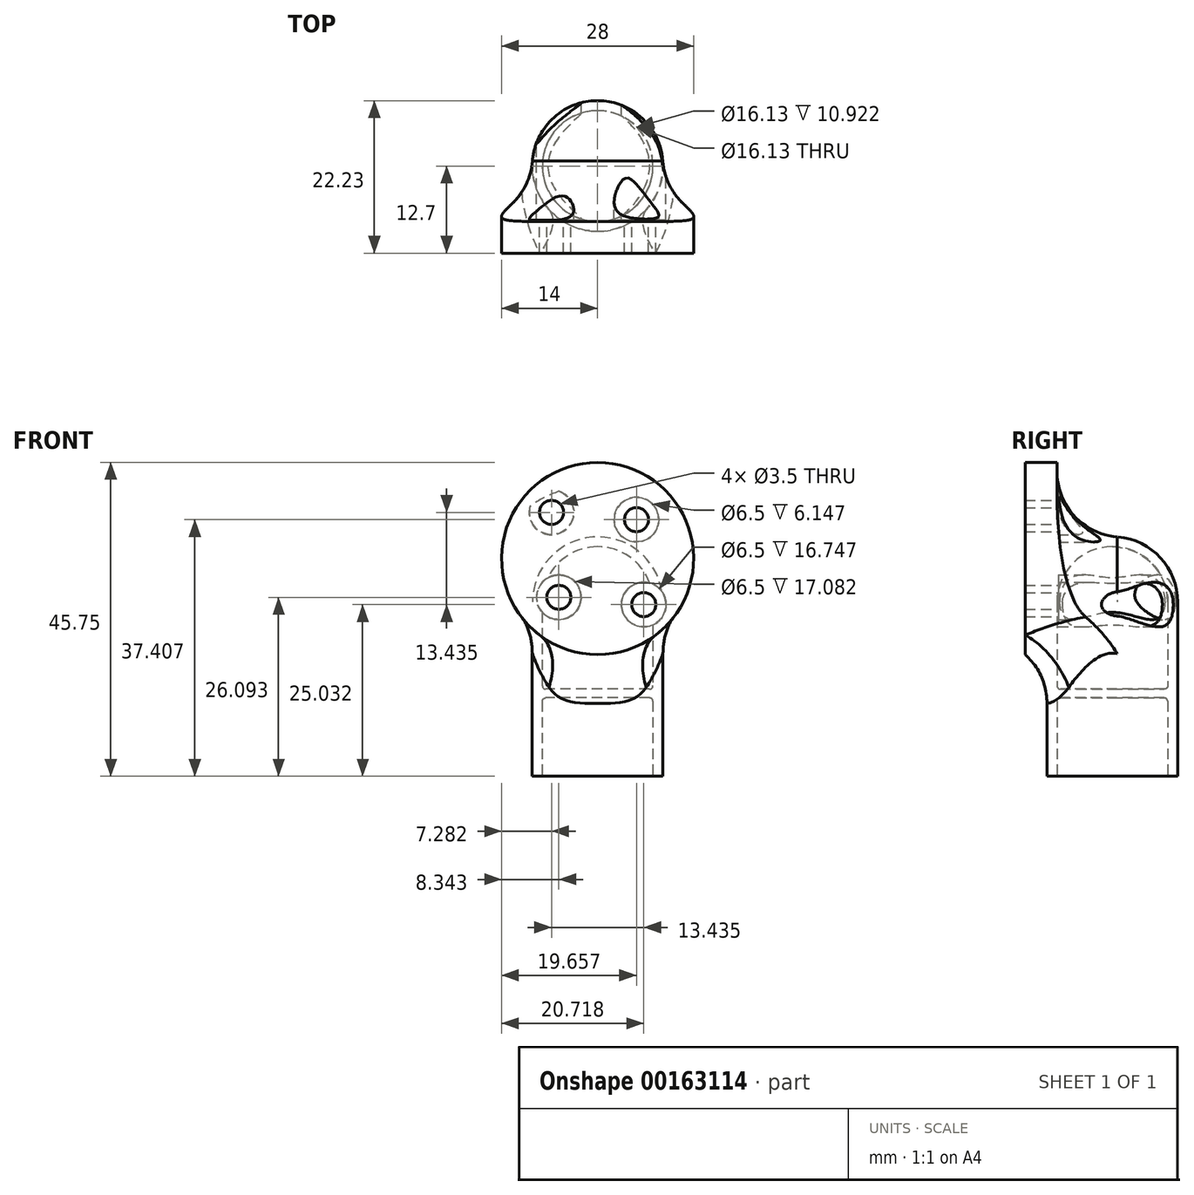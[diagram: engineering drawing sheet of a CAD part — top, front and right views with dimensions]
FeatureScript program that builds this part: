
annotation { "Feature Type Name" : "Feature", "Feature Type Description" : "" }
export const myFeature = defineFeature(function(context is Context, id is Id, definition is map)
    precondition{}
    {
        {
            var Q0;
            Q0=qCreatedBy(makeId("Top.planeOp"),FACE);
            var sketch = newSketch(context, id + "F0", { "sketchPlane" : qUnion([Q0])});
            skCircle(sketch, "E0", {"center": v(0, 0) * mm, "radius": 8.06 * mm});
            skCircle(sketch, "E1", {"center": v(0, 0) * mm, "radius": 9.53 * mm});
            skSolve(sketch);
        }
        {
            var Q0;
            Q0 = qSketchRegion(id + "F0", true);
            extrude(context, id + "F1", {"entities" : qUnion([Q0]), "depth" : 12.7 * mm, "hasSecondDirection" : true, "secondDirectionOppositeDirection" : true, "secondDirectionDepth" : 12.7 * mm});
        }
        {
            var Q0;
            Q0=qCreatedBy(makeId("Front.planeOp"),FACE);
            var sketch = newSketch(context, id + "F2", { "sketchPlane" : qUnion([Q0])});
            skCircle(sketch, "E2", {"center": v(0, 19.05) * mm, "radius": 14 * mm});
            skSolve(sketch);
        }
        {
            var Q0;
            Q0 = qSketchRegion(id + "F2", true);
            extrude(context, id + "F3", {"entities" : qUnion([Q0]), "operationType" : NewBodyOperationType.ADD, "depth" : 12.7 * mm, "hasSecondDirection" : true, "secondDirectionOppositeDirection" : false, "secondDirectionDepth" : 16.13 * mm / 2});
        }
        {
            var Q0;
            Q0=qCreatedBy(makeId("Right.planeOp"),FACE);
            var sketch = newSketch(context, id + "F4", { "sketchPlane" : qUnion([Q0])});
            skLineSegment(sketch, "E3", {"start": v(0, 0) * mm, "end": v(0, 38.72) * mm, "construction": true});
            skArc(sketch, "E4", {"start": v(9.53, 12.7) * mm, "mid": v(6.74, 19.44) * mm, "end": v(0, 22.23) * mm});
            skArc(sketch, "E5", {"start": v(0, 20.76) * mm, "mid": v(5.7, 18.4) * mm, "end": v(8.06, 12.7) * mm});
            skLineSegment(sketch, "E6", {"start": v(9.53, 12.7) * mm, "end": v(8.06, 12.7) * mm});
            skLineSegment(sketch, "E7", {"start": v(0, 22.23) * mm, "end": v(0, 20.76) * mm});
            skSolve(sketch);
        }
        {
            var Q0;
            Q0=qCreatedBy(makeId("Right.planeOp"),FACE);
            var sketch = newSketch(context, id + "F5", { "sketchPlane" : qUnion([Q0])});
            skLineSegment(sketch, "E8", {"start": v(0, 0) * mm, "end": v(0, 27.06) * mm});
            skSolve(sketch);
        }
        {
            var Q0;
            Q0=makeQuery(id+"F4.imprint","IMPRINT",FACE,{"disambiguationData":[TD([[makeQuery(id+"F4.imprint","IMPRINT",EDGE,{"derivedFrom":sQuery(id+"F4.wireOp",EDGE,"E4")}),1.0]])]});
            var Q1;
            Q1=sQuery(id+"F5.wireOp",EDGE,"E8");
            revolve(context, id + "F6", {"operationType" : NewBodyOperationType.ADD, "entities" : qUnion([Q0]), "axis" : qUnion([Q1]), "revolveType" : RevolveType.FULL});
        }
        {
            var Q0;
            Q0=makeQuery(id+"F3.boolean.opBoolean","INTERSECT",EDGE,{"disambiguationData":[OD(1.0)],"derivedFrom":[makeQuery(id+"F1.opExtrude","SWEPT_FACE",FACE,{"disambiguationData":[OSD([sQuery(id+"F0.wireOp",EDGE,"E1")])]}),makeQuery(id+"F3.opExtrude","CAP_FACE",FACE,{"disambiguationData":[OSD([sQuery(id+"F2.wireOp",EDGE,"E2")])],"isStart":true})]});
            fillet(context, id + "F7", {"entities" : qUnion([Q0]), "radius" : 9.52 * mm, "tangentPropagation" : true, "allowEdgeOverflow" : false});
        }
        {
            var Q0;
            Q0=makeQuery(id+"F3.boolean.opBoolean","INTERSECT",EDGE,{"disambiguationData":[OD(1.0)],"derivedFrom":[makeQuery(id+"F1.opExtrude","SWEPT_FACE",FACE,{"disambiguationData":[OSD([sQuery(id+"F0.wireOp",EDGE,"E1")])]}),makeQuery(id+"F3.opExtrude","SWEPT_FACE",FACE,{"disambiguationData":[OSD([sQuery(id+"F2.wireOp",EDGE,"E2")])]})]});
            var Q1;
            Q1=makeQuery(id+"F3.boolean.opBoolean","INTERSECT",EDGE,{"disambiguationData":[OD(0.0)],"derivedFrom":[makeQuery(id+"F1.opExtrude","SWEPT_FACE",FACE,{"disambiguationData":[OSD([sQuery(id+"F0.wireOp",EDGE,"E1")])]}),makeQuery(id+"F3.opExtrude","SWEPT_FACE",FACE,{"disambiguationData":[OSD([sQuery(id+"F2.wireOp",EDGE,"E2")])]})]});
            fillet(context, id + "F8", {"entities" : qUnion([Q0, Q1]), "radius" : 9.52 * mm, "tangentPropagation" : true, "allowEdgeOverflow" : false});
        }
        {
            var Q0;
            Q0=qCreatedBy(makeId("Front.planeOp"),FACE);
            var sketch = newSketch(context, id + "F9", { "sketchPlane" : qUnion([Q0])});
            skCircle(sketch, "E9", {"center": v(0, 19.05) * mm, "radius": 8 * mm, "construction": true});
            skCircle(sketch, "E10", {"center": v(0, 19.05) * mm, "radius": 9.5 * mm, "construction": true});
            skLineSegment(sketch, "E11", {"start": v(-6.72, 25.77) * mm, "end": v(6.72, 12.33) * mm, "construction": true});
            skLineSegment(sketch, "E12", {"start": v(-5.66, 13.4) * mm, "end": v(5.66, 24.7) * mm, "construction": true});
            skSolve(sketch);
        }
        {
            var Q0;
            Q0=sQuery(id+"F9.wireOp",VERTEX,"E12.end");
            var Q1;
            Q1=sQuery(id+"F9.wireOp",VERTEX,"E11.start");
            var Q2;
            Q2=sQuery(id+"F9.wireOp",VERTEX,"E12.start");
            var Q3;
            Q3=sQuery(id+"F9.wireOp",VERTEX,"E11.end");
            var Q4;
            Q4=makeQuery(id+"F1.opExtrude","SWEPT_BODY",BODY,{"disambiguationData":[OSD([sQuery(id+"F0.wireOp",EDGE,"E0"),sQuery(id+"F0.wireOp",EDGE,"E1")])]});
            hole(context, id + "F10", {"style" : HoleStyle.C_BORE, "endStyle" : HoleEndStyle.THROUGH, "oppositeDirection" : true, "holeDiameter" : 3.5 * mm, "cBoreDiameter" : 6.5 * mm, "cBoreDepth" : 7.87 * mm, "startFromSketch" : true, "locations" : qUnion([Q0, Q1, Q2, Q3]), "scope" : qUnion([Q4]), "isTappedThrough" : true});
        }
        {
            var Q0;
            Q0=sQuery(id+"F9.wireOp",VERTEX,"E11.end");
            var Q1;
            Q1=sQuery(id+"F9.wireOp",VERTEX,"E12.start");
            var Q2;
            Q2=makeQuery(id+"F1.opExtrude","SWEPT_BODY",BODY,{"disambiguationData":[OSD([sQuery(id+"F0.wireOp",EDGE,"E0"),sQuery(id+"F0.wireOp",EDGE,"E1")])]});
            hole(context, id + "F11", {"style" : HoleStyle.SIMPLE, "endStyle" : HoleEndStyle.THROUGH, "holeDiameter" : 6.5 * mm, "locations" : qUnion([Q0, Q1]), "scope" : qUnion([Q2]), "isTappedThrough" : true});
        }
        {
            var Q0;
            Q0=qCreatedBy(makeId("Top.planeOp"),FACE);
            var sketch = newSketch(context, id + "F12", { "sketchPlane" : qUnion([Q0])});
            skCircle(sketch, "E13", {"center": v(0, 0) * mm, "radius": 9.53 * mm});
            skSolve(sketch);
        }
        {
            var Q0;
            Q0 = qSketchRegion(id + "F12", true);
            extrude(context, id + "F13", {"entities" : qUnion([Q0]), "operationType" : NewBodyOperationType.ADD, "oppositeDirection" : true, "depth" : 1.27 * mm});
        }
        {
            var Q0;
            Q0=makeQuery(id+"F13.boolean.opBoolean","INTERSECT",EDGE,{"derivedFrom":[makeQuery(id+"F1.opExtrude","SWEPT_FACE",FACE,{"disambiguationData":[OSD([sQuery(id+"F0.wireOp",EDGE,"E0")])]}),makeQuery(id+"F13.opExtrude","CAP_FACE",FACE,{"disambiguationData":[OSD([sQuery(id+"F12.wireOp",EDGE,"E13")])],"isStart":false})]});
            var Q1;
            Q1=makeQuery(id+"F13.boolean.opBoolean","INTERSECT",EDGE,{"derivedFrom":[makeQuery(id+"F1.opExtrude","SWEPT_FACE",FACE,{"disambiguationData":[OSD([sQuery(id+"F0.wireOp",EDGE,"E0")])]}),makeQuery(id+"F13.opExtrude","CAP_FACE",FACE,{"disambiguationData":[OSD([sQuery(id+"F12.wireOp",EDGE,"E13")])],"isStart":true})]});
            fillet(context, id + "F14", {"entities" : qUnion([Q0, Q1]), "radius" : 0.5 * mm, "tangentPropagation" : true, "allowEdgeOverflow" : false});
        }
    });
